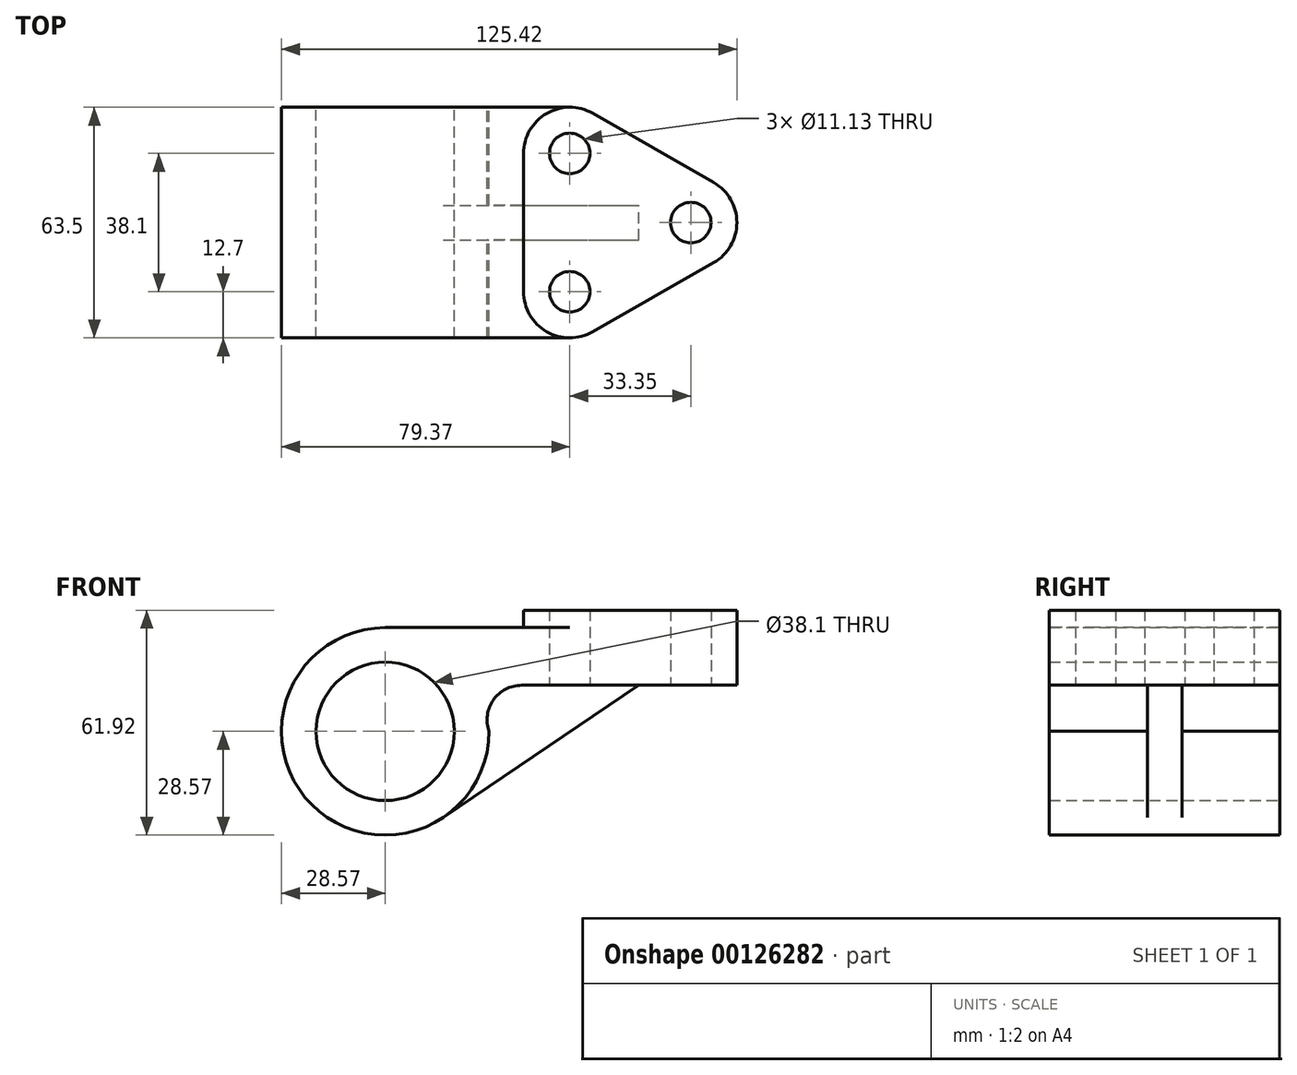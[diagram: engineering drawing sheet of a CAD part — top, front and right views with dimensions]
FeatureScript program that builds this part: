
annotation { "Feature Type Name" : "Feature", "Feature Type Description" : "" }
export const myFeature = defineFeature(function(context is Context, id is Id, definition is map)
    precondition{}
    {
        {
            var Q0;
            Q0=qCreatedBy(makeId("Front.planeOp"),FACE);
            var sketch = newSketch(context, id + "F0", { "sketchPlane" : qUnion([Q0])});
            skCircle(sketch, "E0", {"center": v(0, 0) * mm, "radius": 19.05 * mm});
            skArc(sketch, "E1", {"start": v(0, 28.58) * mm, "mid": v(-20.2, -20.2) * mm, "end": v(28.58, 0) * mm});
            skLineSegment(sketch, "E2", {"start": v(0, 28.58) * mm, "end": v(37.56, 28.58) * mm});
            skArc(sketch, "E3", {"start": v(37.56, 12.7) * mm, "mid": v(29.78, 8.67) * mm, "end": v(28.58, 0) * mm});
            skLineSegment(sketch, "E4", {"start": v(37.56, 12.7) * mm, "end": v(96.3, 12.7) * mm});
            skLineSegment(sketch, "E5", {"start": v(16, -23.68) * mm, "end": v(69.85, 12.7) * mm});
            skLineSegment(sketch, "E6", {"start": v(37.56, 28.58) * mm, "end": v(96.3, 28.58) * mm});
            skLineSegment(sketch, "E7", {"start": v(96.3, 28.58) * mm, "end": v(96.3, 12.7) * mm});
            skSolve(sketch);
        }
        {
            var Q0;
            Q0=makeQuery(id+"F0.imprint","IMPRINT",FACE,{"disambiguationData":[TD([[makeQuery(id+"F0.imprint","IMPRINT",EDGE,{"derivedFrom":sQuery(id+"F0.wireOp",EDGE,"E0")}),-1.0]])]});
            extrude(context, id + "F1", {"entities" : qUnion([Q0]), "endBound" : BoundingType.SYMMETRIC, "depth" : 63.5 * mm});
        }
        {
            var Q0;
            Q0=makeQuery(id+"F1.opExtrude","SWEPT_FACE",FACE,{"disambiguationData":[OSD([sQuery(id+"F0.wireOp",EDGE,"E2"),sQuery(id+"F0.wireOp",EDGE,"E6")])]});
            cPlane(context, id + "F2", {"entities" : qUnion([Q0]), "cplaneType" : CPlaneType.OFFSET, "offset" : 0 * mm, "width" : 152.4 * mm, "height" : 152.4 * mm});
        }
        {
            var Q0;
            Q0=qCreatedBy(id+"F2.planeOp",FACE);
            var sketch = newSketch(context, id + "F3", { "sketchPlane" : qUnion([Q0])});
            skLineSegment(sketch, "E8", {"start": v(-43.42, 0) * mm, "end": v(156.1, 0) * mm, "construction": true});
            skLineSegment(sketch, "E9", {"start": v(57.1, 30.08) * mm, "end": v(90.45, 11.03) * mm});
            skLineSegment(sketch, "E10", {"start": v(57.1, -30.08) * mm, "end": v(90.45, -11.03) * mm});
            skArc(sketch, "E11", {"start": v(90.45, -11.03) * mm, "mid": v(96.85, 0) * mm, "end": v(90.45, 11.03) * mm});
            skArc(sketch, "E12", {"start": v(57.1, 30.08) * mm, "mid": v(44.42, 30.03) * mm, "end": v(38.1, 19.05) * mm});
            skArc(sketch, "E13", {"start": v(38.1, -19.05) * mm, "mid": v(44.42, -30.03) * mm, "end": v(57.1, -30.08) * mm});
            skLineSegment(sketch, "E14", {"start": v(38.1, 19.05) * mm, "end": v(38.1, -19.05) * mm});
            skCircle(sketch, "E15", {"center": v(50.8, 19.05) * mm, "radius": 5.56 * mm});
            skCircle(sketch, "E16", {"center": v(50.8, -19.05) * mm, "radius": 5.56 * mm});
            skCircle(sketch, "E17", {"center": v(84.15, 0) * mm, "radius": 5.56 * mm});
            skSolve(sketch);
        }
        {
            var Q0;
            Q0=makeQuery(id+"F3.imprint","IMPRINT",FACE,{"disambiguationData":[TD([[makeQuery(id+"F3.imprint","IMPRINT",EDGE,{"derivedFrom":sQuery(id+"F3.wireOp",EDGE,"E9")}),-1.0]])]});
            extrude(context, id + "F4", {"entities" : qUnion([Q0]), "operationType" : NewBodyOperationType.ADD, "depth" : 4.78 * mm});
        }
        {
            var Q0;
            {var subQ0=sQuery(id+"F3.wireOp",EDGE,"E9");var subQ2=sQuery(id+"F0.wireOp",EDGE,"E6");var subQ3=sQuery(id+"F0.wireOp",EDGE,"E2");var subQ4=makeQuery(id+"F1.opExtrude","SWEPT_FACE",FACE,{"disambiguationData":[OSD([subQ3,subQ2])]});Q0=makeQuery(id+"F4.boolean.opBoolean","SPLIT",FACE,{"disambiguationData":[TD([makeQuery(id+"F4.opExtrude","SWEPT_FACE",FACE,{"disambiguationData":[OSD([subQ0])]})])],"derivedFrom":subQ4});}
            var Q1;
            {var subQ2=sQuery(id+"F3.wireOp",EDGE,"E10");var subQ4=sQuery(id+"F0.wireOp",EDGE,"E6");var subQ5=sQuery(id+"F0.wireOp",EDGE,"E2");var subQ6=makeQuery(id+"F1.opExtrude","SWEPT_FACE",FACE,{"disambiguationData":[OSD([subQ5,subQ4])]});Q1=makeQuery(id+"F4.boolean.opBoolean","SPLIT",FACE,{"disambiguationData":[TD([makeQuery(id+"F4.opExtrude","SWEPT_FACE",FACE,{"disambiguationData":[OSD([subQ2])]})])],"derivedFrom":subQ6});}
            extrude(context, id + "F5", {"entities" : qUnion([Q0, Q1]), "operationType" : NewBodyOperationType.REMOVE, "endBound" : BoundingType.THROUGH_ALL, "oppositeDirection" : true, "depth" : 25.4 * mm});
        }
        {
            var Q0;
            Q0=makeQuery(id+"F4.opExtrude","CAP_FACE",FACE,{"disambiguationData":[OSD([sQuery(id+"F3.wireOp",EDGE,"E9"),sQuery(id+"F3.wireOp",EDGE,"E10"),sQuery(id+"F3.wireOp",EDGE,"E11"),sQuery(id+"F3.wireOp",EDGE,"E12"),sQuery(id+"F3.wireOp",EDGE,"E13"),sQuery(id+"F3.wireOp",EDGE,"E14"),sQuery(id+"F3.wireOp",EDGE,"E15"),sQuery(id+"F3.wireOp",EDGE,"E16"),sQuery(id+"F3.wireOp",EDGE,"E17")])],"isStart":true});
            extrude(context, id + "F6", {"entities" : qUnion([Q0]), "operationType" : NewBodyOperationType.ADD, "depth" : 15.88 * mm});
        }
        {
            var Q0;
            {var subQ0=sQuery(id+"F0.wireOp",EDGE,"E3");Q0=makeQuery(id+"F0.imprint","IMPRINT",FACE,{"disambiguationData":[TD([[makeQuery(id+"F0.imprint","IMPRINT",EDGE,{"derivedFrom":subQ0}),1.0]])]});}
            extrude(context, id + "F7", {"entities" : qUnion([Q0]), "operationType" : NewBodyOperationType.ADD, "endBound" : BoundingType.SYMMETRIC, "depth" : 9.52 * mm});
        }
        {
            var Q0;
            Q0=makeQuery(id+"F4.boolean.opBoolean","SPLIT",FACE,{"disambiguationData":[TD([makeQuery(id+"F4.opExtrude","SWEPT_FACE",FACE,{"disambiguationData":[OSD([sQuery(id+"F3.wireOp",EDGE,"E16")])]})])],"derivedFrom":makeQuery(id+"F1.opExtrude","SWEPT_FACE",FACE,{"disambiguationData":[OSD([sQuery(id+"F0.wireOp",EDGE,"E2"),sQuery(id+"F0.wireOp",EDGE,"E6")])]})});
            var Q1;
            Q1=makeQuery(id+"F4.boolean.opBoolean","SPLIT",FACE,{"disambiguationData":[TD([makeQuery(id+"F4.opExtrude","SWEPT_FACE",FACE,{"disambiguationData":[OSD([sQuery(id+"F3.wireOp",EDGE,"E15")])]})])],"derivedFrom":makeQuery(id+"F1.opExtrude","SWEPT_FACE",FACE,{"disambiguationData":[OSD([sQuery(id+"F0.wireOp",EDGE,"E2"),sQuery(id+"F0.wireOp",EDGE,"E6")])]})});
            var Q2;
            Q2=makeQuery(id+"F4.boolean.opBoolean","SPLIT",FACE,{"disambiguationData":[TD([makeQuery(id+"F4.opExtrude","SWEPT_FACE",FACE,{"disambiguationData":[OSD([sQuery(id+"F3.wireOp",EDGE,"E17")])]})])],"derivedFrom":makeQuery(id+"F1.opExtrude","SWEPT_FACE",FACE,{"disambiguationData":[OSD([sQuery(id+"F0.wireOp",EDGE,"E2"),sQuery(id+"F0.wireOp",EDGE,"E6")])]})});
            extrude(context, id + "F8", {"entities" : qUnion([Q0, Q1, Q2]), "operationType" : NewBodyOperationType.REMOVE, "endBound" : BoundingType.THROUGH_ALL, "oppositeDirection" : true, "depth" : 25.4 * mm});
        }
    });
